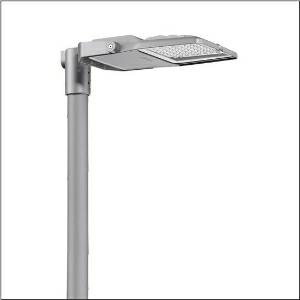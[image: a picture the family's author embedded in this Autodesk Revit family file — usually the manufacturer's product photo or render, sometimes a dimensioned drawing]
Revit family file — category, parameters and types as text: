
# Revit family: floodlight_fl_21_iq_mini___pl61_5xa7772c4c3a_2e37
name_source: partatom
category: Lighting Fixtures
units: mm (PartAtom-declared; Revit-internal decimal feet)

## family parameters
Cut with Voids When Loaded = No
Host = Face
Light Source = No
Part Type = Normal
Room Calculation Point = No
Round Connector Dimension = Use Diameter
Shared = No

## types (1)
- --- (1 x LED, 12490 lm, 87.2 W, 4000K)
    Apparent Load = 87 VA
    CIE Flux Codes = 33 65 98 100 100
    Color Rendering = 70
    Color Temperature = 4000K
    Default Elevation = 1800 mm
    Description = Floodlight FL 21 iQ mini, floodlight, primary light control with lens, of PMMA, primary optical cover: protective disc, of toughened safety glass, transparent, light distribution: PL61, light emission: direct distribution, installation type: surface-mounted, lamps: LED, High Power LED, rated values: 12.490lm | 87,2W | 143,2lm/W (begin service life); end service life: 12.490lm | 92,1W; at 50% lumin. flux: 6.245lm | 40,2W | 155,3lm/W, colour temperature: 4000K, colour rendering: CRI > 70, light colour: 740, light setting 1 begin service life: 100% | 12.490lm | 87,2W | 143,2lm/W | 4.000K, light setting 1 end service life: 92,1W, further light settings possible, control: pre-setting: linear dimming characteristic, Auto-Match, Temp-Guard, Night-Set, Smart-Wire, Desk-Remote (wireless, voltage-free reading and setting of iQ features in the workshop via application-optimized NFC function/RFID function), optimised constant luminous flux control (CLO 2.0), Light-Fading, Lumen-Switch, with terminal, 6-pole, mains connection: 220..240V, AC, 50/60Hz, luminaire housing, of diecast aluminium, powder-coated, SITECO metallic grey (DB 702S), corrosivity category C5 mid according to DIN EN ISO 12944suitable for swimming poolschlorine-resistant, sealing non-destructively replaceable, please order mast flange separately, mast bracket, of steel, galvanised, powder-coated, protection rating (complete): IP66, insulation class (complete): insulation class II (safety insulation), certification: CE, ENEC, VDE, protection symbol: D, impact resistance: IK08, permissible operating ambient temperature: -40..+40°C, permissible operating ambient temperature for outdoor applications: -40..+50°C, standard: DIN EN 12944, LABS conformity tested according to VDMA 24364:2018-05, packaging unit: 1 piece

Light Distribution: PL61
    Height = 70 mm
    Lamp = 1 x LED
    Lamp Light Flux = 12490 lm
    Lamp Power = 87.2 W
    Lamp count = 1
    Length = 485 mm
    Luminous efficacy = 143 lm/W
    Manufacturer = Siteco
    ModVariant = No
    Model = 5XA7772C4C3A
    Number of Poles = 1
    OnlyDefault = Yes
    Power Factor = 1
    Product Name = Floodlight FL 21 iQ mini | PL61
    Product group = floodlight | pylon annexe
    ProductGroupID = 6201
    Protection Class = Protection class II
    Protection Degree = IP 66
    RLX_Detail_Level = 1
    RLX_Emergency_Light_Flux = 0 lm
    RLX_Emergency_Type = 0
    RLX_Emergency_Type_DB = No
    RlxData = <blob elided: 101677 chars, md5=b931cbd7>
    Socket = socket
    Standby Power = 0 W
    System Light Flux = 12490 lm
    System Power = 87 W
    Type Comments = factory setting: luminous flux: 100 % | dim-lin: 254 | 456 mA
    Type Image = l_1007125.jpg
    URL = http://relux.com
    VarID = @adj_172385
    Voltage = 0 V
    Weight = 0.00 kg
    Width = 337 mm

## geometry (parser evidence)
native form markers: Blend x4, Sweep x13
no freeform markers — native parametric forms only
